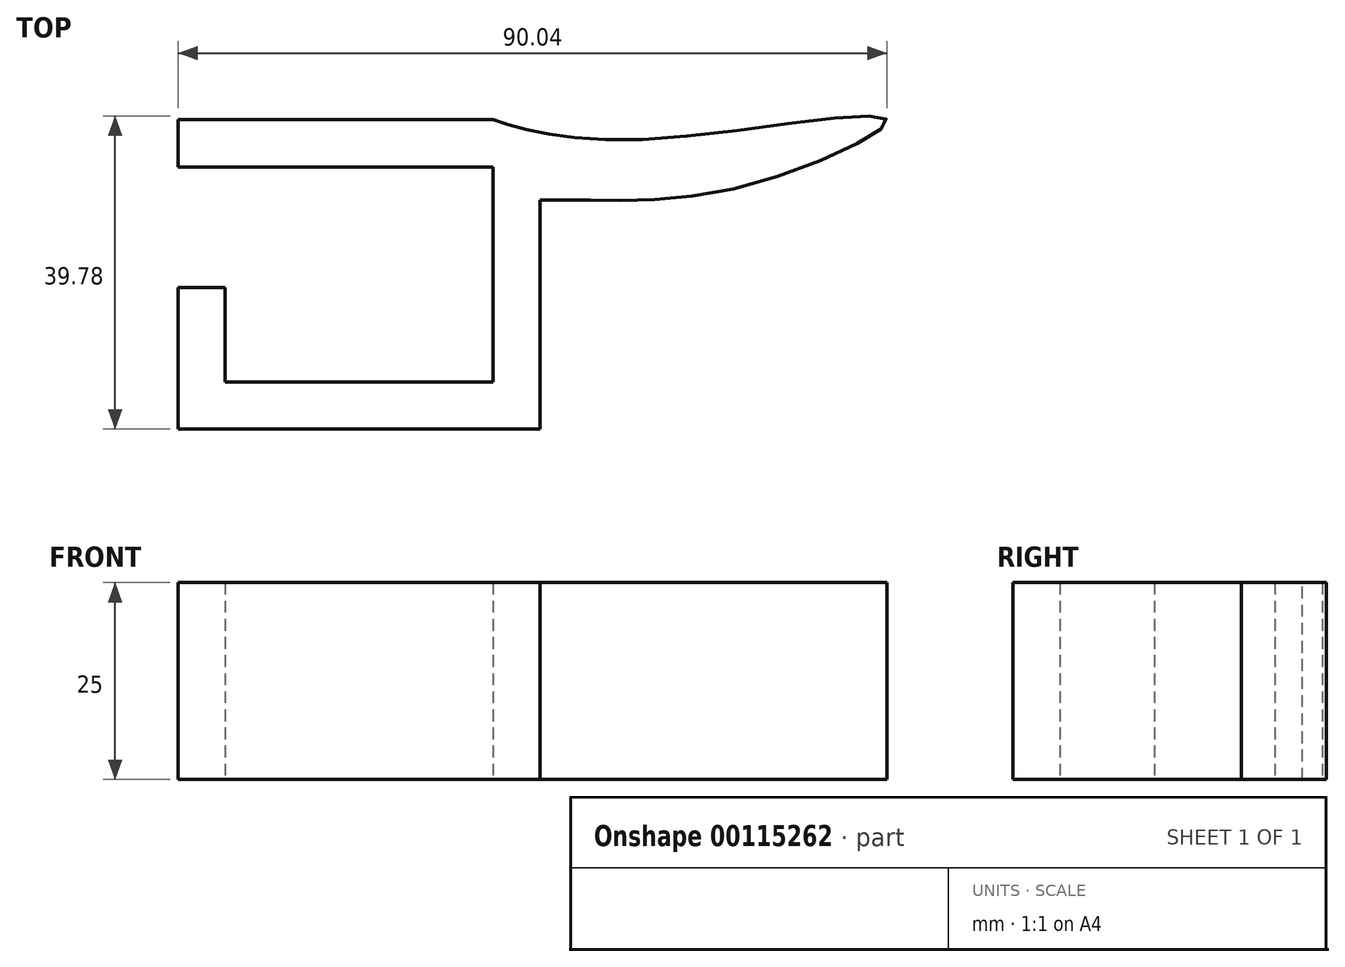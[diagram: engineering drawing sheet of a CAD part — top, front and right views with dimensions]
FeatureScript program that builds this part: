
annotation { "Feature Type Name" : "Feature", "Feature Type Description" : "" }
export const myFeature = defineFeature(function(context is Context, id is Id, definition is map)
    precondition{}
    {
        {
            var Q0;
            Q0=qCreatedBy(makeId("Top.planeOp"),FACE);
            var sketch = newSketch(context, id + "F0", { "sketchPlane" : qUnion([Q0])});
            skLineSegment(sketch, "E0", {"start": v(-40, 19.65) * mm, "end": v(0, 19.65) * mm});
            skLineSegment(sketch, "E1", {"start": v(-40, -19.65) * mm, "end": v(0, -19.65) * mm});
            skLineSegment(sketch, "E2", {"start": v(-40, 19.65) * mm, "end": v(-40, 13.65) * mm});
            skLineSegment(sketch, "E3", {"start": v(-40, 13.65) * mm, "end": v(0, 13.65) * mm});
            skLineSegment(sketch, "E4", {"start": v(0, 13.65) * mm, "end": v(0, 19.65) * mm});
            skLineSegment(sketch, "E5", {"start": v(-40, -19.65) * mm, "end": v(-40, -13.65) * mm});
            skLineSegment(sketch, "E6", {"start": v(-40, -13.65) * mm, "end": v(0, -13.65) * mm});
            skLineSegment(sketch, "E7", {"start": v(0, -13.65) * mm, "end": v(0, -19.65) * mm});
            skFitSpline(sketch, "E8", {"points": [v(0, 19.65) * mm, v(5.5, 18.15) * mm, v(23.4, 17.45) * mm, v(50, 19.65) * mm, v(32.43, 11.35) * mm, v(10.9, 9.45) * mm, v(0, 9.45) * mm], "startDerivative": vector(40.05, -12.74) * mm, "endDerivative": vector(-94.34, 1.26) * mm});
            skLineSegment(sketch, "E9", {"start": v(0, 13.65) * mm, "end": v(0, 9.45) * mm});
            skLineSegment(sketch, "E10", {"start": v(0, -19.65) * mm, "end": v(6, -19.65) * mm});
            skLineSegment(sketch, "E11", {"start": v(6, -19.65) * mm, "end": v(6, 9.45) * mm});
            skLineSegment(sketch, "E12", {"start": v(0, 9.45) * mm, "end": v(0, -13.65) * mm});
            skLineSegment(sketch, "E13", {"start": v(-40, -13.65) * mm, "end": v(-40, -1.65) * mm});
            skLineSegment(sketch, "E14", {"start": v(-40, -1.65) * mm, "end": v(-34, -1.65) * mm});
            skLineSegment(sketch, "E15", {"start": v(-34, -1.65) * mm, "end": v(-34, -13.65) * mm});
            skSolve(sketch);
        }
        {
            var Q0;
            Q0 = qSketchRegion(id + "F0", true);
            extrude(context, id + "F1", {"entities" : qUnion([Q0]), "depth" : 25 * mm});
        }
    });
